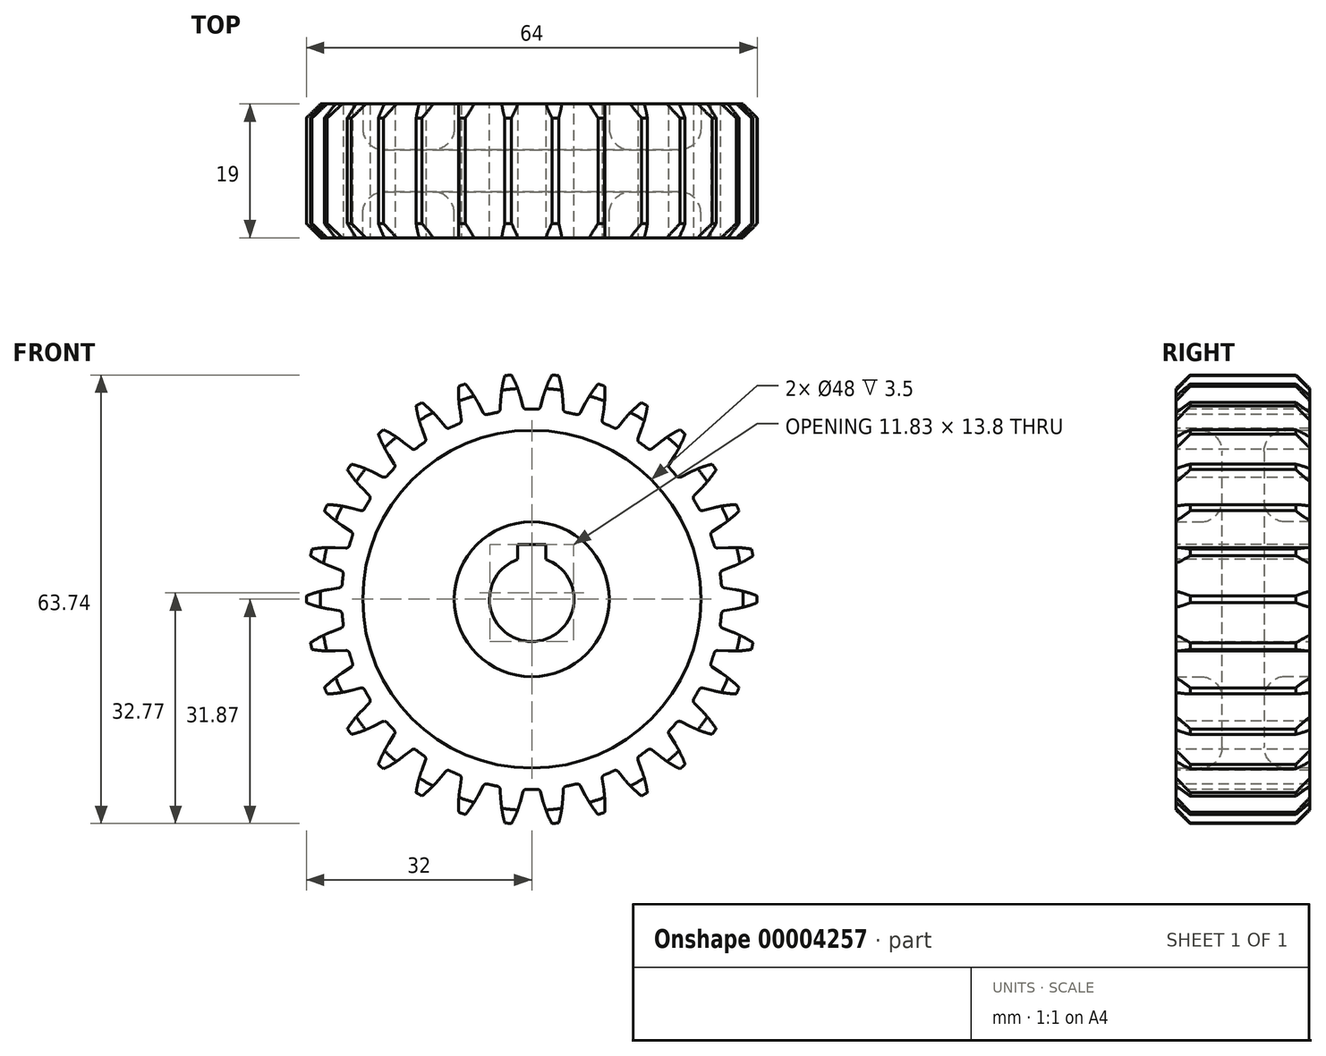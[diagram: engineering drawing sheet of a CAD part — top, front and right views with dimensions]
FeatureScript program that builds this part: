
annotation { "Feature Type Name" : "Feature", "Feature Type Description" : "" }
export const myFeature = defineFeature(function(context is Context, id is Id, definition is map)
    precondition{}
    {
        {
            var Q0;
            Q0=qCreatedBy(makeId("Right.planeOp"),FACE);
            var sketch = newSketch(context, id + "F0", { "sketchPlane" : qUnion([Q0])});
            skLineSegment(sketch, "E0", {"start": v(0, 0) * mm, "end": v(27.39, 0) * mm, "construction": true});
            skLineSegment(sketch, "E1", {"start": v(0, 6) * mm, "end": v(0, 32) * mm});
            skLineSegment(sketch, "E2", {"start": v(0, 32) * mm, "end": v(9.5, 32) * mm});
            skLineSegment(sketch, "E3", {"start": v(9.5, 32) * mm, "end": v(9.5, 24) * mm});
            skLineSegment(sketch, "E4", {"start": v(9.5, 24) * mm, "end": v(3, 24) * mm});
            skLineSegment(sketch, "E5", {"start": v(3, 24) * mm, "end": v(3, 11) * mm});
            skLineSegment(sketch, "E6", {"start": v(3, 11) * mm, "end": v(9.5, 11) * mm});
            skLineSegment(sketch, "E7", {"start": v(9.5, 11) * mm, "end": v(9.5, 6) * mm});
            skLineSegment(sketch, "E8", {"start": v(9.5, 6) * mm, "end": v(0, 6) * mm});
            skSolve(sketch);
        }
        {
            var Q0;
            Q0=makeQuery(id+"F0.imprint","IMPRINT",FACE,{"disambiguationData":[TD([[makeQuery(id+"F0.imprint","IMPRINT",EDGE,{"derivedFrom":sQuery(id+"F0.wireOp",EDGE,"E1")}),-1.0]])]});
            var Q1;
            Q1=sQuery(id+"F0.wireOp",EDGE,"E0");
            revolve(context, id + "F1", {"entities" : qUnion([Q0]), "axis" : qUnion([Q1]), "revolveType" : RevolveType.FULL});
        }
        {
            var Q0;
            Q0=makeQuery(id+"F1.opRevolve","SWEPT_BODY",BODY,{"disambiguationData":[OSD([sQuery(id+"F0.wireOp",EDGE,"E1"),sQuery(id+"F0.wireOp",EDGE,"E2"),sQuery(id+"F0.wireOp",EDGE,"E3"),sQuery(id+"F0.wireOp",EDGE,"E4"),sQuery(id+"F0.wireOp",EDGE,"E5"),sQuery(id+"F0.wireOp",EDGE,"E6"),sQuery(id+"F0.wireOp",EDGE,"E7"),sQuery(id+"F0.wireOp",EDGE,"E8")])]});
            var Q1;
            Q1=makeQuery(id+"F1.opRevolve","SWEPT_FACE",FACE,{"disambiguationData":[OSD([sQuery(id+"F0.wireOp",EDGE,"E1")])]});
            mirror(context, id + "F2", {"entities" : qUnion([Q0]), "mirrorPlane" : qUnion([Q1])});
        }
        {
            var Q0;
            Q0=makeQuery(id+"F2.opPattern","COPY",BODY,{"derivedFrom":makeQuery(id+"F1.opRevolve","SWEPT_BODY",BODY,{"disambiguationData":[OSD([sQuery(id+"F0.wireOp",EDGE,"E1"),sQuery(id+"F0.wireOp",EDGE,"E2"),sQuery(id+"F0.wireOp",EDGE,"E3"),sQuery(id+"F0.wireOp",EDGE,"E4"),sQuery(id+"F0.wireOp",EDGE,"E5"),sQuery(id+"F0.wireOp",EDGE,"E6"),sQuery(id+"F0.wireOp",EDGE,"E7"),sQuery(id+"F0.wireOp",EDGE,"E8")])]}),"instanceName":"1"});
            var Q1;
            Q1=makeQuery(id+"F1.opRevolve","SWEPT_BODY",BODY,{"disambiguationData":[OSD([sQuery(id+"F0.wireOp",EDGE,"E1"),sQuery(id+"F0.wireOp",EDGE,"E2"),sQuery(id+"F0.wireOp",EDGE,"E3"),sQuery(id+"F0.wireOp",EDGE,"E4"),sQuery(id+"F0.wireOp",EDGE,"E5"),sQuery(id+"F0.wireOp",EDGE,"E6"),sQuery(id+"F0.wireOp",EDGE,"E7"),sQuery(id+"F0.wireOp",EDGE,"E8")])]});
            booleanBodies(context, id + "F3", {"operationType" : BooleanOperationType.UNION, "tools" : qUnion([Q0, Q1])});
        }
        {
            var Q0;
            Q0=makeQuery(id+"F1.opRevolve","SWEPT_EDGE",EDGE,{"disambiguationData":[OSD([sQuery(id+"F0.wireOp",EDGE,"E2"),sQuery(id+"F0.wireOp",EDGE,"E3")])]});
            var Q1;
            Q1=makeQuery(id+"F2.opPattern","COPY",EDGE,{"derivedFrom":makeQuery(id+"F1.opRevolve","SWEPT_EDGE",EDGE,{"disambiguationData":[OSD([sQuery(id+"F0.wireOp",EDGE,"E2"),sQuery(id+"F0.wireOp",EDGE,"E3")])]}),"instanceName":"1"});
            chamfer(context, id + "F4", {"entities" : qUnion([Q0, Q1]), "width" : 2 * mm, "tangentPropagation" : true});
        }
        {
            var Q0;
            Q0=makeQuery(id+"F1.opRevolve","SWEPT_EDGE",EDGE,{"disambiguationData":[OSD([sQuery(id+"F0.wireOp",EDGE,"E4"),sQuery(id+"F0.wireOp",EDGE,"E5")])]});
            var Q1;
            Q1=makeQuery(id+"F1.opRevolve","SWEPT_EDGE",EDGE,{"disambiguationData":[OSD([sQuery(id+"F0.wireOp",EDGE,"E5"),sQuery(id+"F0.wireOp",EDGE,"E6")])]});
            var Q2;
            Q2=makeQuery(id+"F2.opPattern","COPY",EDGE,{"derivedFrom":makeQuery(id+"F1.opRevolve","SWEPT_EDGE",EDGE,{"disambiguationData":[OSD([sQuery(id+"F0.wireOp",EDGE,"E4"),sQuery(id+"F0.wireOp",EDGE,"E5")])]}),"instanceName":"1"});
            var Q3;
            Q3=makeQuery(id+"F2.opPattern","COPY",EDGE,{"derivedFrom":makeQuery(id+"F1.opRevolve","SWEPT_EDGE",EDGE,{"disambiguationData":[OSD([sQuery(id+"F0.wireOp",EDGE,"E5"),sQuery(id+"F0.wireOp",EDGE,"E6")])]}),"instanceName":"1"});
            fillet(context, id + "F5", {"entities" : qUnion([Q0, Q1, Q2, Q3]), "radius" : 3 * mm, "tangentPropagation" : true, "allowEdgeOverflow" : false});
        }
        {
            var Q0;
            Q0=makeQuery(id+"F2.opPattern","COPY",FACE,{"derivedFrom":makeQuery(id+"F1.opRevolve","SWEPT_FACE",FACE,{"disambiguationData":[OSD([sQuery(id+"F0.wireOp",EDGE,"E7")])]}),"instanceName":"1"});
            var sketch = newSketch(context, id + "F6", { "sketchPlane" : qUnion([Q0])});
            skLineSegment(sketch, "E9.bottom", {"start": v(-2, 5.66) * mm, "end": v(2, 5.66) * mm});
            skLineSegment(sketch, "E9.top", {"start": v(-2, 7.8) * mm, "end": v(2, 7.8) * mm});
            skLineSegment(sketch, "E9.left", {"start": v(-2, 5.66) * mm, "end": v(-2, 7.8) * mm});
            skLineSegment(sketch, "E9.right", {"start": v(2, 5.66) * mm, "end": v(2, 7.8) * mm});
            skSolve(sketch);
        }
        {
            var Q0;
            Q0 = qSketchRegion(id + "F6", true);
            extrude(context, id + "F7", {"entities" : qUnion([Q0]), "operationType" : NewBodyOperationType.REMOVE, "endBound" : BoundingType.THROUGH_ALL, "oppositeDirection" : true, "depth" : 25 * mm});
        }
        {
            var Q0;
            Q0=makeQuery(id+"F2.opPattern","COPY",FACE,{"derivedFrom":makeQuery(id+"F1.opRevolve","SWEPT_FACE",FACE,{"disambiguationData":[OSD([sQuery(id+"F0.wireOp",EDGE,"E3")])]}),"instanceName":"1"});
            var sketch = newSketch(context, id + "F8", { "sketchPlane" : qUnion([Q0])});
            skCircle(sketch, "E10", {"center": v(0, 0) * mm, "radius": 30 * mm, "construction": true});
            skLineSegment(sketch, "E11", {"start": v(0, 0) * mm, "end": v(0, 32) * mm, "construction": true});
            skArc(sketch, "E12.0", {"start": v(2.87, 31.87) * mm, "mid": v(0, 32) * mm, "end": v(-2.87, 31.87) * mm});
            skArc(sketch, "E13", {"start": v(-1.64, 28.82) * mm, "mid": v(-2.17, 30.38) * mm, "end": v(-2.87, 31.87) * mm});
            skArc(sketch, "E14.0.MirrorCS", {"start": v(1.64, 28.82) * mm, "mid": v(2.17, 30.38) * mm, "end": v(2.87, 31.87) * mm});
            skLineSegment(sketch, "E15", {"start": v(-2, 29.93) * mm, "end": v(-2.71, 31.89) * mm, "construction": true});
            skPoint(sketch, "E16", {"position": v(2, 29.93) * mm});
            skLineSegment(sketch, "E17", {"start": v(-1.64, 28.82) * mm, "end": v(-1.13, 26.98) * mm});
            skArc(sketch, "E18", {"start": v(1.13, 26.98) * mm, "mid": v(0, 27) * mm, "end": v(-1.13, 26.98) * mm});
            skLineSegment(sketch, "E19", {"start": v(1.64, 28.82) * mm, "end": v(1.13, 26.98) * mm});
            skSolve(sketch);
        }
        {
            var Q0;
            Q0 = qSketchRegion(id + "F8", true);
            extrude(context, id + "F9", {"entities" : qUnion([Q0]), "operationType" : NewBodyOperationType.REMOVE, "endBound" : BoundingType.THROUGH_ALL, "oppositeDirection" : true, "depth" : 25 * mm});
        }
        {
            var Q0;
            Q0=makeQuery(id+"F9.boolean.opBoolean","COPY",EDGE,{"derivedFrom":makeQuery(id+"F9.opExtrude","SWEPT_EDGE",EDGE,{"disambiguationData":[OSD([sQuery(id+"F8.wireOp",EDGE,"E17"),sQuery(id+"F8.wireOp",EDGE,"E18")])]})});
            var Q1;
            Q1=makeQuery(id+"F9.boolean.opBoolean","COPY",EDGE,{"derivedFrom":makeQuery(id+"F9.opExtrude","SWEPT_EDGE",EDGE,{"disambiguationData":[OSD([sQuery(id+"F8.wireOp",EDGE,"E18"),sQuery(id+"F8.wireOp",EDGE,"E19")])]})});
            var Q2;
            Q2=makeQuery(id+"F9.boolean.opBoolean","COPY",EDGE,{"derivedFrom":makeQuery(id+"F9.opExtrude","SWEPT_EDGE",EDGE,{"disambiguationData":[OSD([sQuery(id+"F8.wireOp",EDGE,"E12.0"),sQuery(id+"F8.wireOp",EDGE,"E13")])]})});
            var Q3;
            Q3=makeQuery(id+"F9.boolean.opBoolean","COPY",EDGE,{"derivedFrom":makeQuery(id+"F9.opExtrude","SWEPT_EDGE",EDGE,{"disambiguationData":[OSD([sQuery(id+"F8.wireOp",EDGE,"E12.0"),sQuery(id+"F8.wireOp",EDGE,"E14.0.MirrorCS")])]})});
            fillet(context, id + "F10", {"entities" : qUnion([Q0, Q1, Q2, Q3]), "radius" : .5 * mm, "tangentPropagation" : true, "allowEdgeOverflow" : false});
        }
        {
            var Q0;
            Q0=makeQuery(id+"F9.boolean.opBoolean","COPY",FACE,{"derivedFrom":makeQuery(id+"F9.opExtrude","SWEPT_FACE",FACE,{"disambiguationData":[OSD([sQuery(id+"F8.wireOp",EDGE,"E13")])]})});
            var Q1;
            Q1=makeQuery(id+"F9.boolean.opBoolean","COPY",FACE,{"derivedFrom":makeQuery(id+"F9.opExtrude","SWEPT_FACE",FACE,{"disambiguationData":[OSD([sQuery(id+"F8.wireOp",EDGE,"E17")])]})});
            var Q2;
            Q2=makeQuery(id+"F9.boolean.opBoolean","COPY",FACE,{"derivedFrom":makeQuery(id+"F9.opExtrude","SWEPT_FACE",FACE,{"disambiguationData":[OSD([sQuery(id+"F8.wireOp",EDGE,"E18")])]})});
            var Q3;
            Q3=makeQuery(id+"F9.boolean.opBoolean","COPY",FACE,{"derivedFrom":makeQuery(id+"F9.opExtrude","SWEPT_FACE",FACE,{"disambiguationData":[OSD([sQuery(id+"F8.wireOp",EDGE,"E19")])]})});
            var Q4;
            Q4=makeQuery(id+"F9.boolean.opBoolean","COPY",FACE,{"derivedFrom":makeQuery(id+"F9.opExtrude","SWEPT_FACE",FACE,{"disambiguationData":[OSD([sQuery(id+"F8.wireOp",EDGE,"E14.0.MirrorCS")])]})});
            var Q5;
            Q5=makeQuery(id+"F10.opFillet","BLEND_FACE",FACE,{"disambiguationData":[OSD([sQuery(id+"F8.wireOp",EDGE,"E12.0"),sQuery(id+"F8.wireOp",EDGE,"E13")])]});
            var Q6;
            Q6=makeQuery(id+"F10.opFillet","BLEND_FACE",FACE,{"disambiguationData":[OSD([sQuery(id+"F8.wireOp",EDGE,"E17"),sQuery(id+"F8.wireOp",EDGE,"E18")])]});
            var Q7;
            Q7=makeQuery(id+"F10.opFillet","BLEND_FACE",FACE,{"disambiguationData":[OSD([sQuery(id+"F8.wireOp",EDGE,"E18"),sQuery(id+"F8.wireOp",EDGE,"E19")])]});
            var Q8;
            Q8=makeQuery(id+"F10.opFillet","BLEND_FACE",FACE,{"disambiguationData":[OSD([sQuery(id+"F8.wireOp",EDGE,"E12.0"),sQuery(id+"F8.wireOp",EDGE,"E14.0.MirrorCS")])]});
            var Q9;
            Q9=makeQuery(id+"F2.opPattern","COPY",FACE,{"derivedFrom":makeQuery(id+"F1.opRevolve","SWEPT_FACE",FACE,{"disambiguationData":[OSD([sQuery(id+"F0.wireOp",EDGE,"E6")])]}),"instanceName":"1"});
            circularPattern(context, id + "F11", {"faces" : qUnion([Q0, Q1, Q2, Q3, Q4, Q5, Q6, Q7, Q8]), "axis" : qUnion([Q9]), "angle" : 360 * degree, "instanceCount" : 30, "equalSpace" : true, "patternType" : PatternType.FACE});
        }
    });
